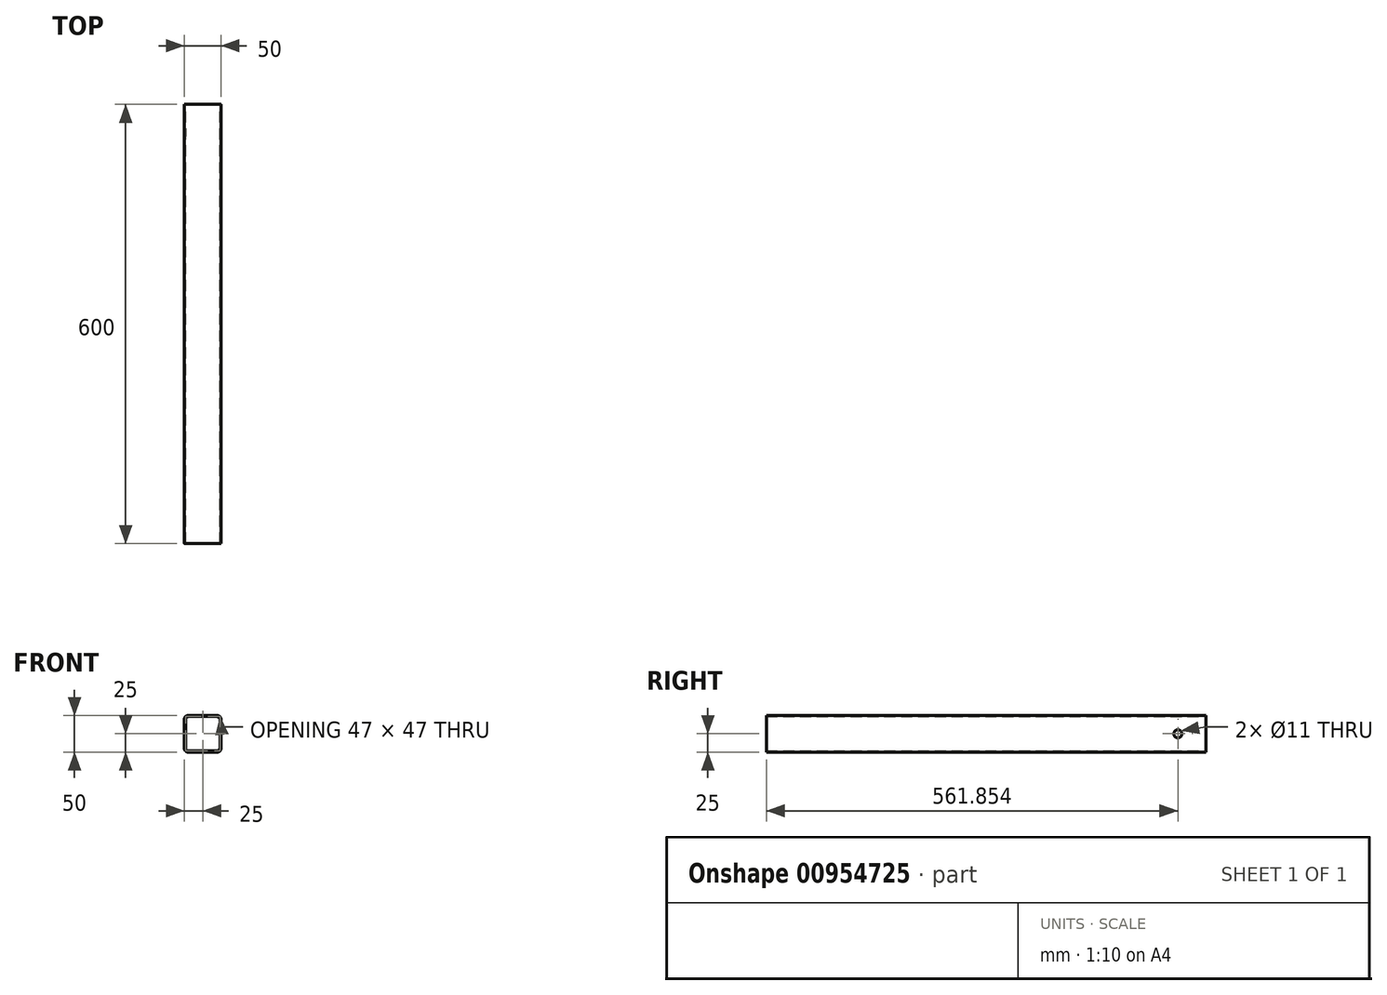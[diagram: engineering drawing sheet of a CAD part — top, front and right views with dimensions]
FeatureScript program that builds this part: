
annotation { "Feature Type Name" : "Feature", "Feature Type Description" : "" }
export const myFeature = defineFeature(function(context is Context, id is Id, definition is map)
    precondition{}
    {
        {
            var Q0;
            Q0=qCreatedBy(makeId("Front.planeOp"),FACE);
            var sketch = newSketch(context, id + "F0", { "sketchPlane" : qUnion([Q0])});
            skLineSegment(sketch, "E0.bottom", {"start": v(7.02, 0) * mm, "end": v(47.02, 0) * mm});
            skLineSegment(sketch, "E0.top", {"start": v(7.02, 50) * mm, "end": v(47.02, 50) * mm});
            skLineSegment(sketch, "E0.left", {"start": v(2.02, 5) * mm, "end": v(2.02, 45) * mm});
            skLineSegment(sketch, "E0.right", {"start": v(52.02, 5) * mm, "end": v(52.02, 45) * mm});
            skLineSegment(sketch, "E1.0", {"start": v(3.52, 5.5) * mm, "end": v(3.52, 44.5) * mm});
            skLineSegment(sketch, "E1.1", {"start": v(7.52, 1.5) * mm, "end": v(46.52, 1.5) * mm});
            skLineSegment(sketch, "E1.2", {"start": v(50.52, 5.5) * mm, "end": v(50.52, 44.5) * mm});
            skLineSegment(sketch, "E1.3", {"start": v(7.52, 48.5) * mm, "end": v(46.52, 48.5) * mm});
            skPoint(sketch, "E2.visualSharp", {"position": v(2.02, 50) * mm});
            skArc(sketch, "E2.filletArc", {"start": v(7.02, 50) * mm, "mid": v(3.48, 48.54) * mm, "end": v(2.02, 45) * mm});
            skPoint(sketch, "E3.visualSharp", {"position": v(52.02, 50) * mm});
            skArc(sketch, "E3.filletArc", {"start": v(52.02, 45) * mm, "mid": v(50.56, 48.54) * mm, "end": v(47.02, 50) * mm});
            skPoint(sketch, "E4.visualSharp", {"position": v(52.02, 0) * mm});
            skArc(sketch, "E4.filletArc", {"start": v(47.02, 0) * mm, "mid": v(50.56, 1.46) * mm, "end": v(52.02, 5) * mm});
            skPoint(sketch, "E5.visualSharp", {"position": v(2.02, 0) * mm});
            skArc(sketch, "E5.filletArc", {"start": v(2.02, 5) * mm, "mid": v(3.48, 1.46) * mm, "end": v(7.02, 0) * mm});
            skPoint(sketch, "E6.visualSharp", {"position": v(3.52, 48.5) * mm});
            skArc(sketch, "E6.filletArc", {"start": v(7.52, 48.5) * mm, "mid": v(4.7, 47.33) * mm, "end": v(3.52, 44.5) * mm});
            skPoint(sketch, "E7.visualSharp", {"position": v(50.52, 48.5) * mm});
            skArc(sketch, "E7.filletArc", {"start": v(50.52, 44.5) * mm, "mid": v(49.35, 47.33) * mm, "end": v(46.52, 48.5) * mm});
            skPoint(sketch, "E8.visualSharp", {"position": v(50.52, 1.5) * mm});
            skArc(sketch, "E8.filletArc", {"start": v(46.52, 1.5) * mm, "mid": v(49.35, 2.67) * mm, "end": v(50.52, 5.5) * mm});
            skPoint(sketch, "E9.visualSharp", {"position": v(3.52, 1.5) * mm});
            skArc(sketch, "E9.filletArc", {"start": v(3.52, 5.5) * mm, "mid": v(4.7, 2.67) * mm, "end": v(7.52, 1.5) * mm});
            skSolve(sketch);
        }
        {
            var Q0;
            Q0=makeQuery(id+"F0.imprint","IMPRINT",FACE,{"disambiguationData":[TD([[makeQuery(id+"F0.imprint","IMPRINT",EDGE,{"derivedFrom":sQuery(id+"F0.wireOp",EDGE,"E0.bottom")}),1.0]])]});
            extrude(context, id + "F1", {"entities" : qUnion([Q0]), "depth" : 600 * mm, "offsetDistance" : 25 * mm});
        }
        {
            var Q0;
            Q0=makeQuery(id+"F1.opExtrude","SWEPT_FACE",FACE,{"disambiguationData":[OSD([sQuery(id+"F0.wireOp",EDGE,"E0.right")])]});
            var sketch = newSketch(context, id + "F2", { "sketchPlane" : qUnion([Q0])});
            skCircle(sketch, "E10", {"center": v(-38.15, 25) * mm, "radius": 5.5 * mm});
            skSolve(sketch);
        }
        {
            var Q0;
            Q0=makeQuery(id+"F2.imprint","IMPRINT",FACE,{"disambiguationData":[TD([[makeQuery(id+"F2.imprint","IMPRINT",EDGE,{"derivedFrom":sQuery(id+"F2.wireOp",EDGE,"E10")}),1.0]])]});
            extrude(context, id + "F3", {"entities" : qUnion([Q0]), "operationType" : NewBodyOperationType.REMOVE, "oppositeDirection" : true, "depth" : 100 * mm, "offsetDistance" : 25 * mm});
        }
    });
